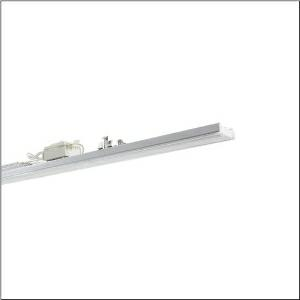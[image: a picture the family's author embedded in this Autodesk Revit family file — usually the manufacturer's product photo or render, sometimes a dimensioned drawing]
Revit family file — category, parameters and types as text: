
# Revit family: licross_r__11_recessed_ho_51tl12dn1d5m_3b99
name_source: partatom
category: Lighting Fixtures
units: mm (PartAtom-declared; Revit-internal decimal feet)

## family parameters
Cut with Voids When Loaded = No
Host = Face
Light Source = No
Part Type = Normal
Room Calculation Point = No
Round Connector Dimension = Use Diameter
Shared = No

## types (1)
- --- (1 x LED, 13580 lm, 76.8 W, 3500K)
    Apparent Load = 77 VA
    CIE Flux Codes = 66 91 98 100 100
    Color Rendering = 80
    Color Temperature = 3500K
    Default Elevation = 1800 mm
    Description = Licross® 11 Recessed HO, luminaire insert, of sheet steel, coil coated, white, length: 1.500mm, width: 66mm, height: 67mm, LED rated luminous flux: 13.580lm, light colour: 835, control gear: DALI 2, with plug, 5-pole, with phase selection, mains connection: 220..240V, AC, 50/60Hz, rated input power: 77W, internal wiring halogen-free, primary optical cover: cover, of PMMA, light emission: direct distribution, primary light characteristic: symmetric, protection rating (complete): IP40, insulation class (complete): insulation class I (protective earthing), certification: CE, ENEC, VDE, UKCA, protection symbol: D if used in an environment without relevant dust loads with corresponding accessories, impact resistance: IK06, permissible ambient temperature for indoor applications: -25..+30°C, corresponds to IFS (International Featured Standards) requirements for safety and quality in the food industry, reducing of maximum allowable ambient temperature of 5°C with ceiling mounting, LABS conformity tested according to VDMA 24364:2018-05, packaging unit: 1 piece
    Height = 58 mm
    Lamp = 1 x LED
    Lamp Light Flux = 13580 lm
    Lamp Power = 76.8 W
    Lamp count = 1
    Length = 1500 mm
    Luminous efficacy = 177 lm/W
    Manufacturer = Siteco
    ModVariant = No
    Model = 51TL12DN1D5M
    Mounting Place = Ceiling
    Mounting Type = Pendant
    Number of Poles = 1
    OnlyDefault = Yes
    Power Factor = 1
    Product Name = Licross® 11 Recessed HO
    Product group = luminaire insert | ceiling pendant
    ProductGroupID = 902
    Protection Class = Protection class I
    Protection Degree = IP 40
    RLX_Detail_Level = 1
    RLX_Emergency_Light_Flux = 0 lm
    RLX_Emergency_Type = 0
    RLX_Emergency_Type_DB = No
    RlxData = <blob elided: 24649 chars, md5=7d71f7be>
    Socket = socket
    Standby Power = 0 W
    System Light Flux = 13580 lm
    System Power = 77 W
    Type Comments = factory setting: luminous flux: 100 % | dim-lin: 254 | 522 mA
    Type Image = l_1296930.jpg
    URL = http://relux.com
    VarID = @adj_089147
    Voltage = 0 V
    Weight = 0.00 kg
    Width = 66 mm

## geometry (parser evidence)
native form markers: Blend x4, Sweep x11
no freeform markers — native parametric forms only
